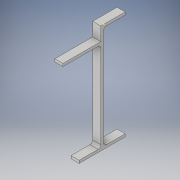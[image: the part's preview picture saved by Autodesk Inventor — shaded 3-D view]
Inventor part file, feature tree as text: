
AUTODESK INVENTOR PART (.ipt)
format: ipt  version: 2017 (Build 210142000, 142)  size: 146,944 bytes
history: native  units: in
note: dims shown in document units (in); Inventor stores cm internally (conversion verified against a paired STEP export)
features: sketch x6, extrude x5, fillet x2
ambient origin geometry x8: Origin, YZ Plane, XZ Plane, XY Plane, X Axis, Y Axis, Z Axis, Center Point
bodies: Solid1 (feature_tree)
feature tree (13):
  extrude  "Extrusion1"  Depth=10.0in
  sketch  "Sketch4"  dims[d2=0.25in d3=0.0in d4=1.25in]
  extrude  "Extrusion2"  Depth=1.25in
  extrude  "Extrusion3"  Depth=3.5in TaperAngle=0.0deg
  fillet  "Fillet2"  Radius=0.25in
  extrude  "Extrusion4"  Depth=0.25in
  extrude  "Extrusion5"  Depth=0.25in
  fillet  "Fillet3"  Radius=2.0in
  sketch  "Sketch3"  dims[d0=0.75in d1=10.0in]
  sketch  "Sketch5"  dims[d5=0.25in d6=3.5in d7=0.0in d8=0.25in]
  sketch  "Sketch6"  dims[d9=2.0in d10=0.0in d12=0.25in]
  sketch  "Sketch7"  dims[d13=0.75in d14=0.25in d15=2.0in d16=0.0in]
  sketch  "Sketch8"  dims[d17=0.25in d18=2.0in d19=0.0in d20=0.25in]
